# Revit family: ДВО-09 30 Вт Грильято DALI
name_source: partatom
category: Осветительные приборы
units: mm (PartAtom-declared; Revit-internal decimal feet)

## family parameters
Всегда вертикально = Да
Заголовок OmniClass = Luminaries for Internal Lighting
Источник света = Да
Номер OmniClass = 23.80.70.11
Общий = Нет
Основа = Потолок
При загрузке вырезать с полостями = Нет
Размер круглого соединителя = Использовать диаметр
Тип детали = Нормальный
Точка расчета площади = Нет

## types (6) — shared parameters
ADSK_Размер_Высота = 45 мм
ADSK_Размер_Длина = 588 мм
ADSK_Размер_Ширина = 588 мм
URL = http://innolux.pro
Блок аварийного питания = нет
Бренд светодиодов = EDISON
Вес светильника = 2.6 кг
Время импульса пускового тока = 4.8 мс
Гарантия = 7 лет
Диапазон рабочих температур = - 20 + 40°C
Диммирование = да
Изготовитель = INNOLUX
Индекс цветопередачи = >80
Класс защиты от поражения током = I
Класс светораспределения по ГОСТ 54350-2011 = П
Климатическое исполнение = УХЛ 4
Кол-во светодиодов = 72
Количество в упаковке = 4
Количество модулей = 4
Коэффициент мощности = >0.95
>0.95
>0.95
Коэффициент пульсации = <5%
Материал корпуса = Металл, окрашенный, белый, матовый
Материал рассеивателя = Полистирол
Напряжение = 176-264 В
Объём упаковки = 0.22*0.61*0.61 м
Полная установленная мощность = 30 В·А
Потребляемый ток = 0
Пусковой ток = 12.2 А
Светофильтр = 16777215
Сила тока = 0.14 А
Смещение цветовой температуры при затухании лампы = <Нет>
Способ монтажа = Встраиваемый / Накладной
Срок службы = 80000
Степень защиты (IP) = 40
Тип кривой силы света по ГОСТ 54350-2011 = Д
Типоразмер светодиода = 2835
Угол наклона = 90.00°
Цвет корпуса = Белый
Частота сети = 50 / 60 Гц

## per-type parameters (varying)
| type | Артикул | Габаритная яркость | Категория по ограничению яркости | Световой поток модуля | Тип рассеивателя | Файл фотометрической сетки | Эффективность светильника |
| ДВО-09-П-30-3К-IP40-Грильято-DALI | 14938 |  | 3 | 1156 | призма | INNOLUX 14 938 DVO-09-P-30-3K-IP40-DALI.ies | 143 |
| ДВО-09-П-30-4К-IP40-Грильято-DALI | 14942 |  | 3 | 1156 | призма | INNOLUX 14 942 DVO-09-P-30-4K-IP40-DALI.ies | 143 |
| ДВО-09-П-30-5К-IP40-Грильято-DALI | 14946 |  | 3 | 1156 | призма | INNOLUX 14 946 DVO-09-P-30-5K-IP40-DALI.ies | 143 |
| ДВО-09-О-30-3К-IP40-Грильято-DALI | 14950 | <5000 кд / м2 | 1 | 1078 | опал | INNOLUX 14 950 DVO-09-O-30-3K-IP40-DALI.ies | 123 |
| ДВО-09-О-30-4К-IP40-Грильято-DALI | 14954 | <5000 кд / м2 | 1 | 1078 | опал | INNOLUX 14 954 DVO-09-O-30-4K-IP40-DALI.ies | 123 |
| ДВО-09-О-30-5К-IP40-Грильято-DALI | 14958 | <5000 кд / м2 | 1 | 1078 | опал | INNOLUX 14 958 DVO-09-O-30-5K-IP40-DALI.ies | 123 |
